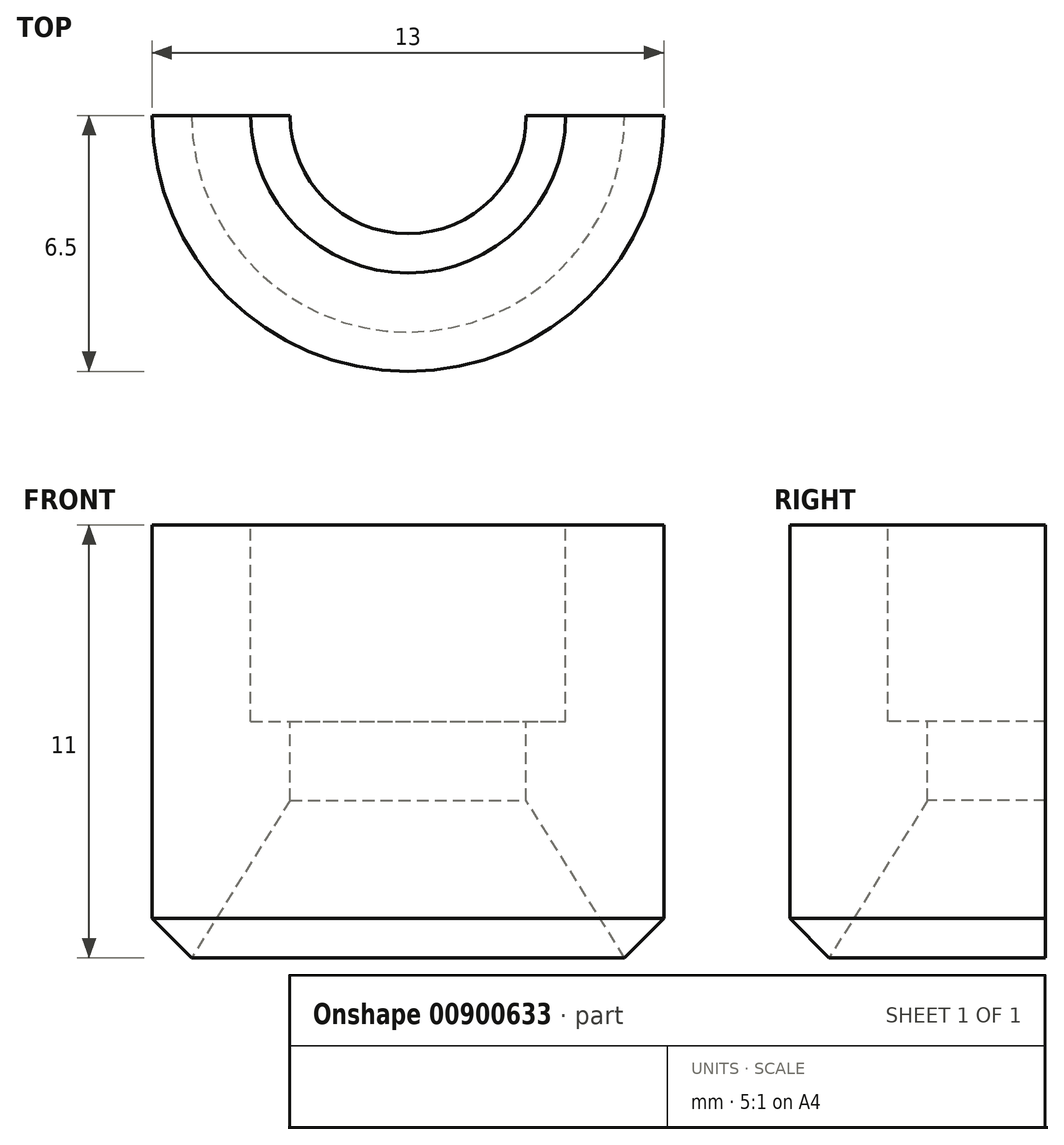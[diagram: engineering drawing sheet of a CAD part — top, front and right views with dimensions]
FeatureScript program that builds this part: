
annotation { "Feature Type Name" : "Feature", "Feature Type Description" : "" }
export const myFeature = defineFeature(function(context is Context, id is Id, definition is map)
    precondition{}
    {
        {
            var Q0;
            Q0=qCreatedBy(makeId("Front.planeOp"),FACE);
            var sketch = newSketch(context, id + "F0", { "sketchPlane" : qUnion([Q0])});
            skLineSegment(sketch, "E0.bottom", {"start": v(26.14, 4.36) * mm, "end": v(28.64, 4.36) * mm});
            skLineSegment(sketch, "E0.left", {"start": v(25.14, -0.64) * mm, "end": v(25.14, -2.64) * mm});
            skLineSegment(sketch, "E0.right", {"start": v(28.64, 4.36) * mm, "end": v(28.64, -5.64) * mm});
            skLineSegment(sketch, "E1", {"start": v(22.14, 6.91) * mm, "end": v(22.14, -13.9) * mm, "construction": true});
            skLineSegment(sketch, "E2.bottom", {"start": v(25.14, -0.64) * mm, "end": v(26.14, -0.64) * mm});
            skLineSegment(sketch, "E2.right", {"start": v(26.14, -0.64) * mm, "end": v(26.14, 4.36) * mm});
            skLineSegment(sketch, "E3", {"start": v(25.14, -2.64) * mm, "end": v(27.64, -6.64) * mm});
            skLineSegment(sketch, "E4", {"start": v(27.64, -6.64) * mm, "end": v(28.64, -5.64) * mm});
            skPoint(sketch, "E5.orphan", {"position": v(28.64, -6.64) * mm});
            skSolve(sketch);
        }
        {
            var Q0;
            Q0=makeQuery(id+"F0.imprint","IMPRINT",FACE,{"disambiguationData":[TD([[makeQuery(id+"F0.imprint","IMPRINT",EDGE,{"derivedFrom":sQuery(id+"F0.wireOp",EDGE,"E0.bottom")}),-1.0]])]});
            var Q1;
            Q1=sQuery(id+"F0.wireOp",EDGE,"E1");
            revolve(context, id + "F1", {"surfaceOperationType" : NewSurfaceOperationType.NEW, "entities" : qUnion([Q0]), "axis" : qUnion([Q1]), "revolveType" : RevolveType.FULL});
        }
        {
            var Q0;
            Q0=qCreatedBy(makeId("Front.planeOp"),FACE);
            var sketch = newSketch(context, id + "F2", { "sketchPlane" : qUnion([Q0])});
            skLineSegment(sketch, "E6.bottom", {"start": v(-5.33, 27.07) * mm, "end": v(48.52, 27.07) * mm});
            skLineSegment(sketch, "E6.top", {"start": v(-5.33, -22.75) * mm, "end": v(48.52, -22.75) * mm});
            skLineSegment(sketch, "E6.left", {"start": v(-5.33, 27.07) * mm, "end": v(-5.33, -22.75) * mm});
            skLineSegment(sketch, "E6.right", {"start": v(48.52, 27.07) * mm, "end": v(48.52, -22.75) * mm});
            skSolve(sketch);
        }
        {
            var Q0;
            Q0=makeQuery(id+"F2.imprint","IMPRINT",FACE,{"disambiguationData":[TD([[makeQuery(id+"F2.imprint","IMPRINT",EDGE,{"derivedFrom":sQuery(id+"F2.wireOp",EDGE,"E6.bottom")}),-1.0]])]});
            extrude(context, id + "F3", {"entities" : qUnion([Q0]), "operationType" : NewBodyOperationType.REMOVE, "endBound" : BoundingType.THROUGH_ALL, "oppositeDirection" : true, "depth" : 25 * mm, "offsetDistance" : 25 * mm});
        }
    });
